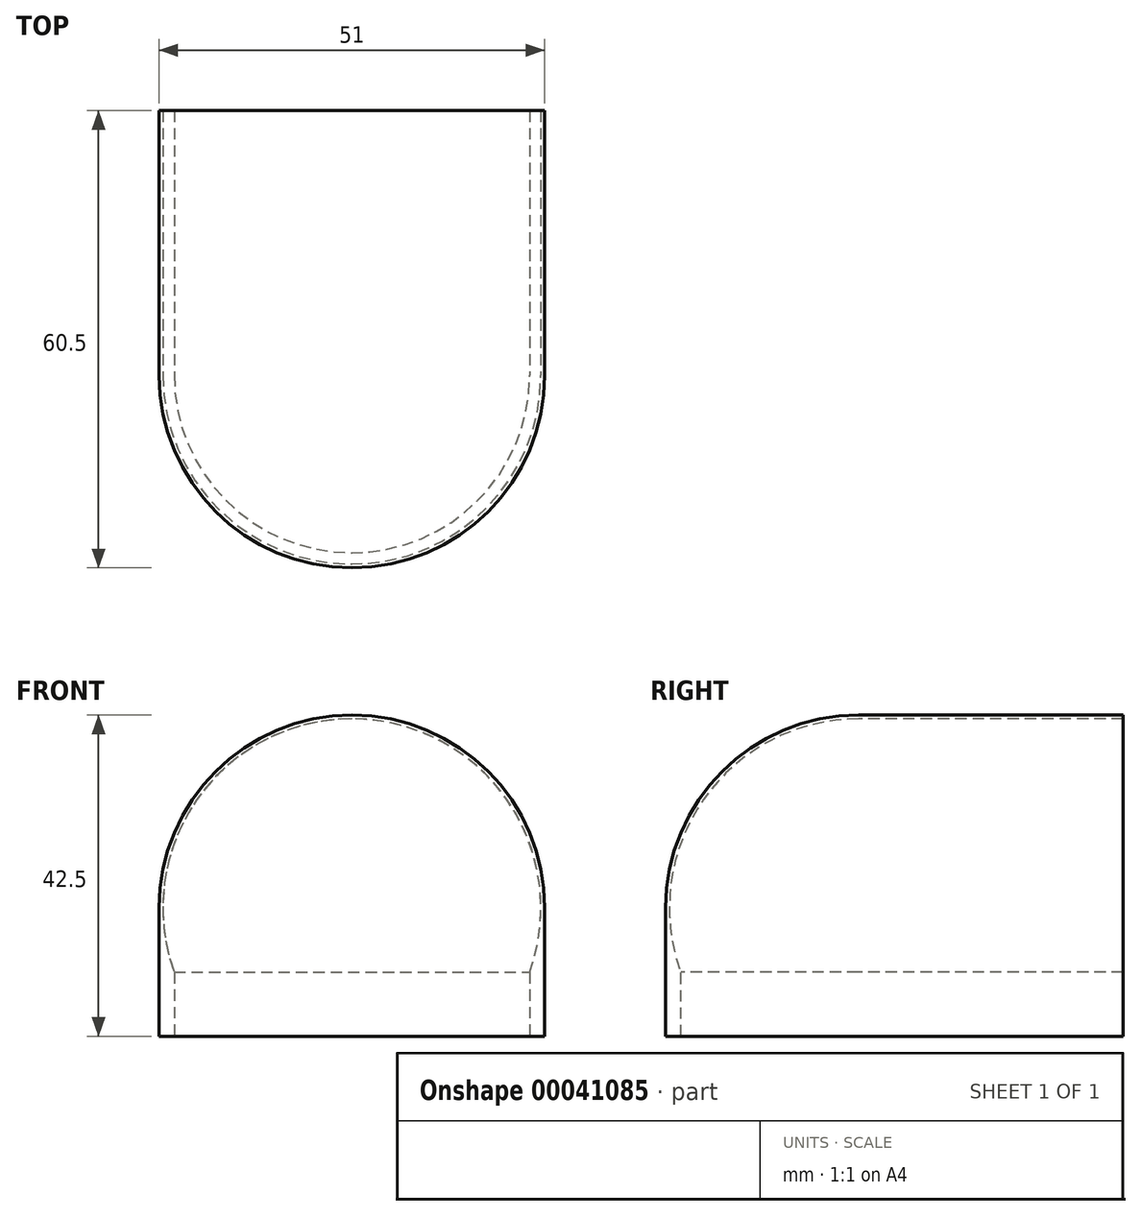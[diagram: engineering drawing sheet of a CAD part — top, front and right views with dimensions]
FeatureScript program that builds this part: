
annotation { "Feature Type Name" : "Feature", "Feature Type Description" : "" }
export const myFeature = defineFeature(function(context is Context, id is Id, definition is map)
    precondition{}
    {
        {
            var Q0;
            Q0=qCreatedBy(makeId("Front.planeOp"),FACE);
            var sketch = newSketch(context, id + "F0", { "sketchPlane" : qUnion([Q0])});
            skArc(sketch, "E0", {"start": v(25, 0) * mm, "mid": v(17.68, 17.68) * mm, "end": v(0, 25) * mm});
            skArc(sketch, "E1", {"start": v(25.5, 0) * mm, "mid": v(18.03, 18.03) * mm, "end": v(0, 25.5) * mm});
            skLineSegment(sketch, "E2", {"start": v(0, 25.5) * mm, "end": v(0, 25) * mm});
            skLineSegment(sketch, "E3", {"start": v(25, 0) * mm, "end": v(25.5, 0) * mm});
            skLineSegment(sketch, "E4", {"start": v(0, 11.64) * mm, "end": v(0, 8.08) * mm, "construction": true});
            skLineSegment(sketch, "E5.bottom", {"start": v(25.5, 0) * mm, "end": v(25, 0) * mm});
            skLineSegment(sketch, "E5.top", {"start": v(25.5, -17) * mm, "end": v(23.5, -17) * mm});
            skLineSegment(sketch, "E5.left", {"start": v(25.5, 0) * mm, "end": v(25.5, -17) * mm});
            skLineSegment(sketch, "E5.right", {"start": v(23.5, -8.53) * mm, "end": v(23.5, -17) * mm});
            skArc(sketch, "E6", {"start": v(25, 0) * mm, "mid": v(24.62, -4.33) * mm, "end": v(23.5, -8.53) * mm});
            skSolve(sketch);
        }
        {
            var Q0;
            Q0 = qSketchRegion(id + "F0", true);
            var Q1;
            Q1=sQuery(id+"F0.wireOp",EDGE,"E4");
            revolve(context, id + "F1", {"entities" : qUnion([Q0]), "axis" : qUnion([Q1]), "revolveType" : RevolveType.ONE_DIRECTION, "angle" : 180 * degree});
        }
        {
            var Q0;
            Q0=makeQuery(id+"F1.opRevolve","CAP_FACE",FACE,{"disambiguationData":[OSD([sQuery(id+"F0.wireOp",EDGE,"E0"),sQuery(id+"F0.wireOp",EDGE,"E1"),sQuery(id+"F0.wireOp",EDGE,"E2"),sQuery(id+"F0.wireOp",EDGE,"E5.top"),sQuery(id+"F0.wireOp",EDGE,"E5.left"),sQuery(id+"F0.wireOp",EDGE,"E5.right"),sQuery(id+"F0.wireOp",EDGE,"E6")])],"isStart":true});
            var sketch = newSketch(context, id + "F2", { "sketchPlane" : qUnion([Q0])});
            skArc(sketch, "E7", {"start": v(-25.5, 0) * mm, "mid": v(0, 25.5) * mm, "end": v(25.5, 0) * mm});
            skArc(sketch, "E8", {"start": v(-23.5, -8.53) * mm, "mid": v(0, 25) * mm, "end": v(23.5, -8.53) * mm});
            skLineSegment(sketch, "E9", {"start": v(-23.5, -8.53) * mm, "end": v(-23.5, -17) * mm});
            skLineSegment(sketch, "E10", {"start": v(-23.5, -17) * mm, "end": v(-25.5, -17) * mm});
            skLineSegment(sketch, "E11", {"start": v(-25.5, -17) * mm, "end": v(-25.5, 0) * mm});
            skLineSegment(sketch, "E12", {"start": v(25.5, -17) * mm, "end": v(25.5, 0) * mm});
            skLineSegment(sketch, "E13", {"start": v(25.5, -17) * mm, "end": v(23.5, -17) * mm});
            skLineSegment(sketch, "E14", {"start": v(23.5, -8.53) * mm, "end": v(23.5, -17) * mm});
            skSolve(sketch);
        }
        {
            var Q0;
            Q0 = qSketchRegion(id + "F2", true);
            extrude(context, id + "F3", {"entities" : qUnion([Q0]), "operationType" : NewBodyOperationType.ADD, "depth" : 35 * mm});
        }
    });
